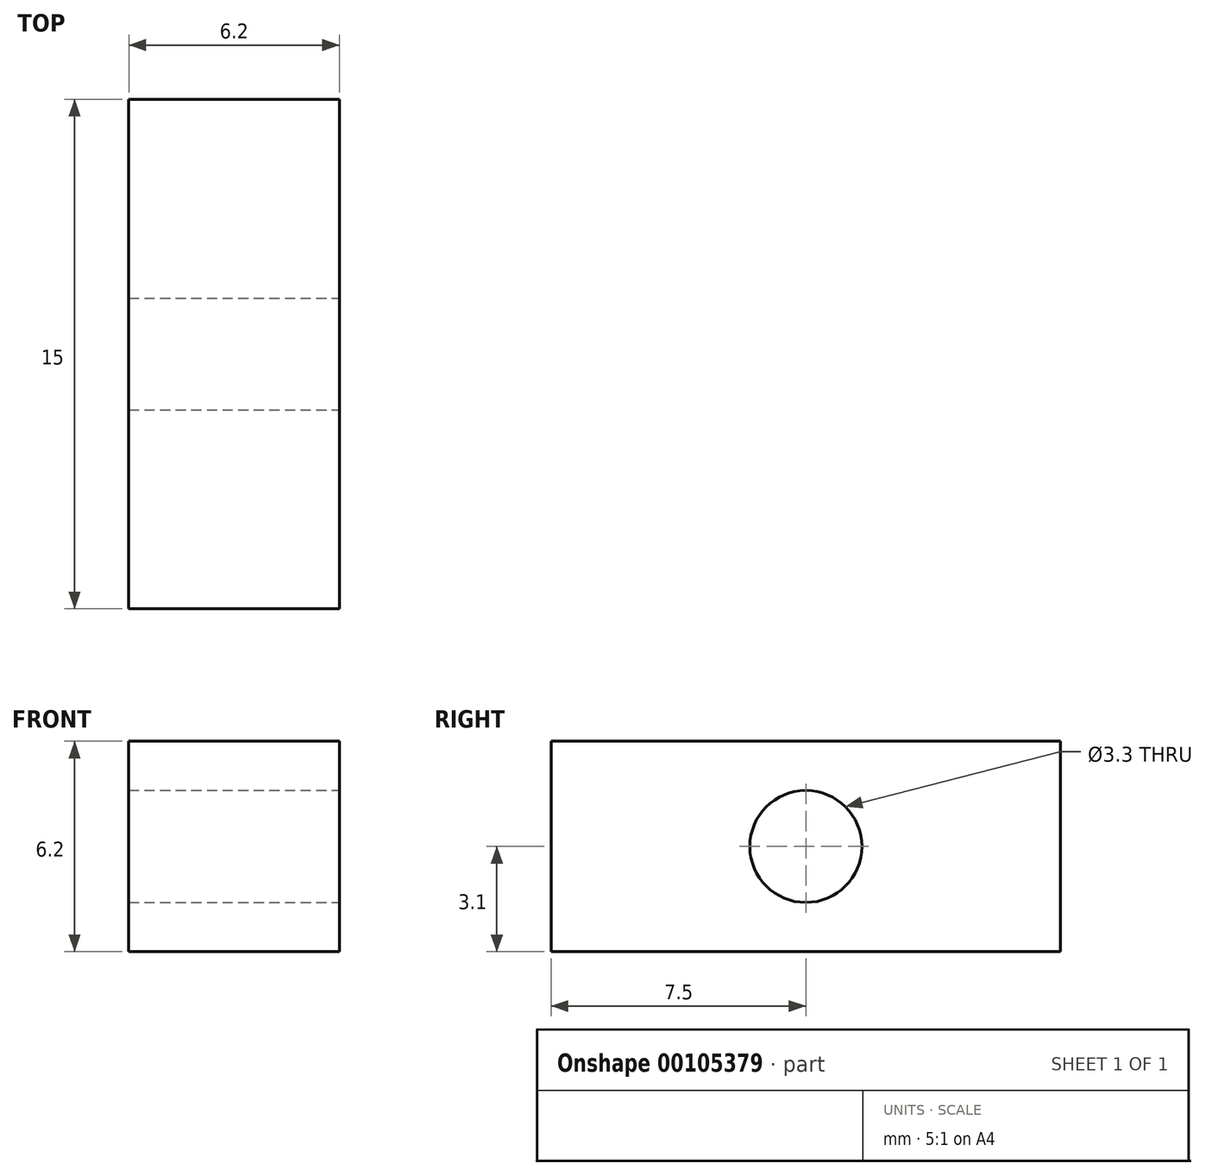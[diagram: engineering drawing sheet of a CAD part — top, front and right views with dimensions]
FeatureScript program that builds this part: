
annotation { "Feature Type Name" : "Feature", "Feature Type Description" : "" }
export const myFeature = defineFeature(function(context is Context, id is Id, definition is map)
    precondition{}
    {
        {
            var Q0;
            Q0=qCreatedBy(makeId("Front.planeOp"),FACE);
            var sketch = newSketch(context, id + "F0", { "sketchPlane" : qUnion([Q0])});
            skLineSegment(sketch, "E0.bottom", {"start": v(19.64, 0) * mm, "end": v(25.84, 0) * mm});
            skLineSegment(sketch, "E0.top", {"start": v(19.64, -6.2) * mm, "end": v(25.84, -6.2) * mm});
            skLineSegment(sketch, "E0.left", {"start": v(19.64, 0) * mm, "end": v(19.64, -6.2) * mm});
            skLineSegment(sketch, "E0.right", {"start": v(25.84, 0) * mm, "end": v(25.84, -6.2) * mm});
            skSolve(sketch);
        }
        {
            var Q0;
            Q0=makeQuery(id+"F0.imprint","IMPRINT",FACE,{"disambiguationData":[TD([[makeQuery(id+"F0.imprint","IMPRINT",EDGE,{"derivedFrom":sQuery(id+"F0.wireOp",EDGE,"AzUvCDoc-ibw3-S6HG-w51a-cNGuq6Fe5iIr.bottom")}),-1.0]])]});
            var Q1;
            Q1=makeQuery(id+"F0.imprint","IMPRINT",FACE,{"disambiguationData":[TD([[makeQuery(id+"F0.imprint","IMPRINT",EDGE,{"derivedFrom":sQuery(id+"F0.wireOp",EDGE,"E0.bottom")}),-1.0]])]});
            extrude(context, id + "F1", {"entities" : qUnion([Q0, Q1]), "depth" : 15 * mm});
        }
        {
            var Q0;
            Q0=makeQuery(id+"F1.opExtrude","SWEPT_FACE",FACE,{"disambiguationData":[OSD([sQuery(id+"F0.wireOp",EDGE,"E0.right")])]});
            var sketch = newSketch(context, id + "F2", { "sketchPlane" : qUnion([Q0])});
            skLineSegment(sketch, "E1", {"start": v(-15, -3.1) * mm, "end": v(0, -3.1) * mm, "construction": true});
            skLineSegment(sketch, "E2", {"start": v(-7.5, 0) * mm, "end": v(-7.5, -6.2) * mm, "construction": true});
            skCircle(sketch, "E3", {"center": v(-7.5, -3.1) * mm, "radius": 1.65 * mm});
            skSolve(sketch);
        }
        {
            var Q0;
            Q0=makeQuery(id+"F2.imprint","IMPRINT",FACE,{"disambiguationData":[TD([[makeQuery(id+"F2.imprint","IMPRINT",EDGE,{"derivedFrom":sQuery(id+"F2.wireOp",EDGE,"E3")}),1.0]])]});
            var Q1;
            Q1=makeQuery(id+"F1.opExtrude","SWEPT_FACE",FACE,{"disambiguationData":[OSD([sQuery(id+"F0.wireOp",EDGE,"E0.left")])]});
            extrude(context, id + "F3", {"entities" : qUnion([Q0]), "operationType" : NewBodyOperationType.REMOVE, "endBound" : BoundingType.UP_TO_SURFACE, "oppositeDirection" : true, "endBoundEntityFace" : qUnion([Q1]), "depth" : 25 * mm});
        }
    });
